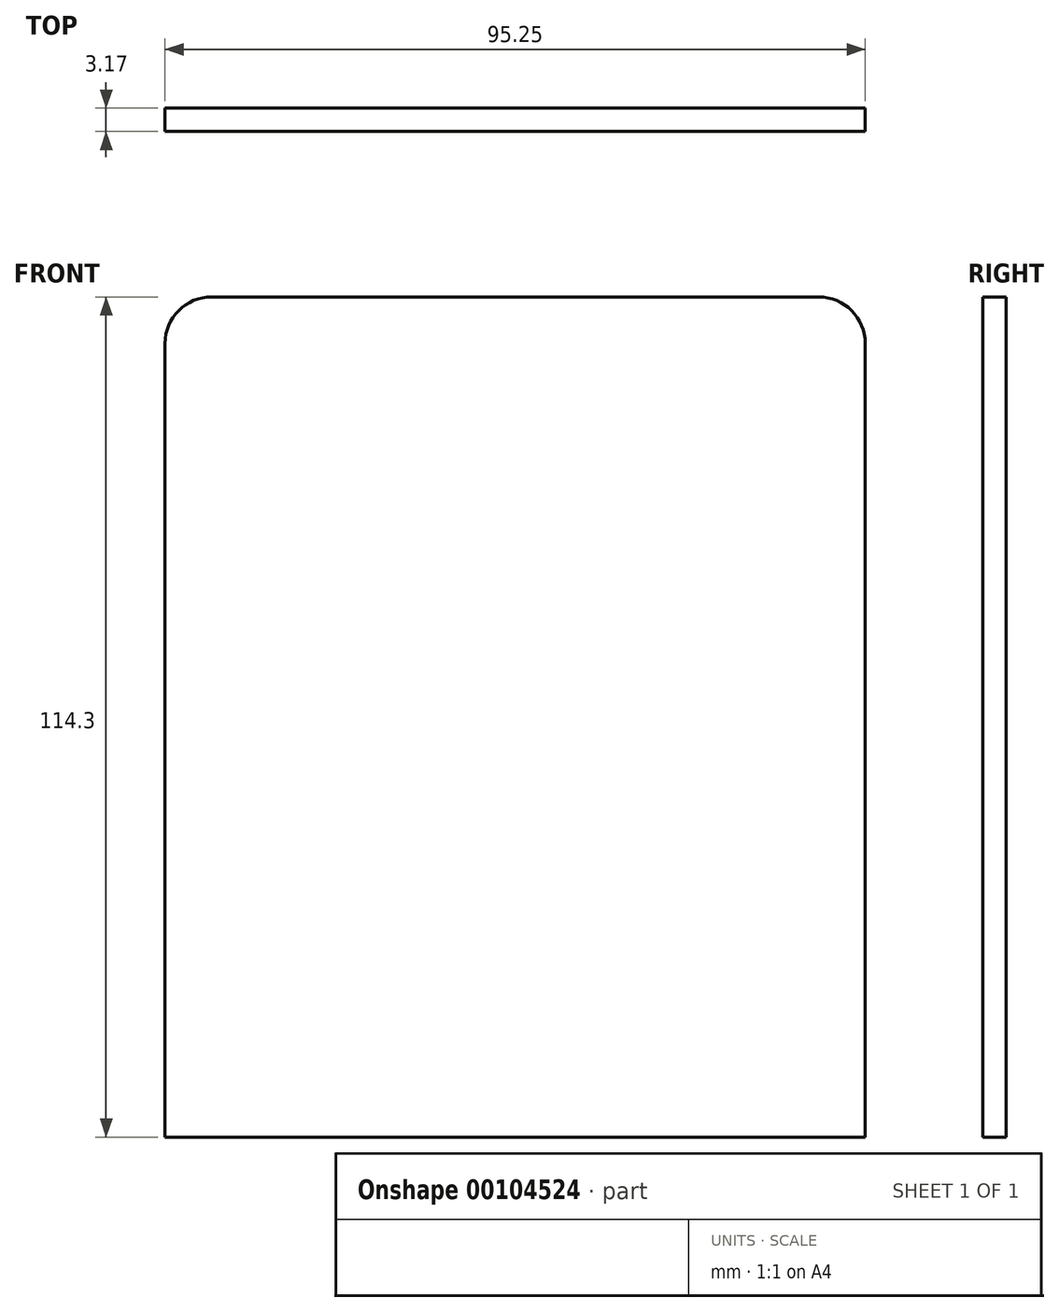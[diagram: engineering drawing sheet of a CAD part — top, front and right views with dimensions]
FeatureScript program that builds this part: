
annotation { "Feature Type Name" : "Feature", "Feature Type Description" : "" }
export const myFeature = defineFeature(function(context is Context, id is Id, definition is map)
    precondition{}
    {
        {
            var Q0;
            Q0=qCreatedBy(makeId("Front.planeOp"),FACE);
            var sketch = newSketch(context, id + "F0", { "sketchPlane" : qUnion([Q0])});
            skLineSegment(sketch, "E0.bottom", {"start": v(0, 0) * mm, "end": v(95.25, 0) * mm});
            skLineSegment(sketch, "E0.top", {"start": v(6.35, 114.3) * mm, "end": v(88.9, 114.3) * mm});
            skLineSegment(sketch, "E0.left", {"start": v(0, 0) * mm, "end": v(0, 107.95) * mm});
            skLineSegment(sketch, "E0.right", {"start": v(95.25, 0) * mm, "end": v(95.25, 107.95) * mm});
            skPoint(sketch, "E1.visualSharp", {"position": v(0, 114.3) * mm});
            skArc(sketch, "E1.filletArc", {"start": v(6.35, 114.3) * mm, "mid": v(1.86, 112.44) * mm, "end": v(0, 107.95) * mm});
            skPoint(sketch, "E2.visualSharp", {"position": v(95.25, 114.3) * mm});
            skArc(sketch, "E2.filletArc", {"start": v(95.25, 107.95) * mm, "mid": v(93.4, 112.44) * mm, "end": v(88.9, 114.3) * mm});
            skSolve(sketch);
        }
        {
            var Q0;
            Q0 = qSketchRegion(id + "F0", true);
            extrude(context, id + "F1", {"entities" : qUnion([Q0]), "depth" : 3.17 * mm});
        }
    });
